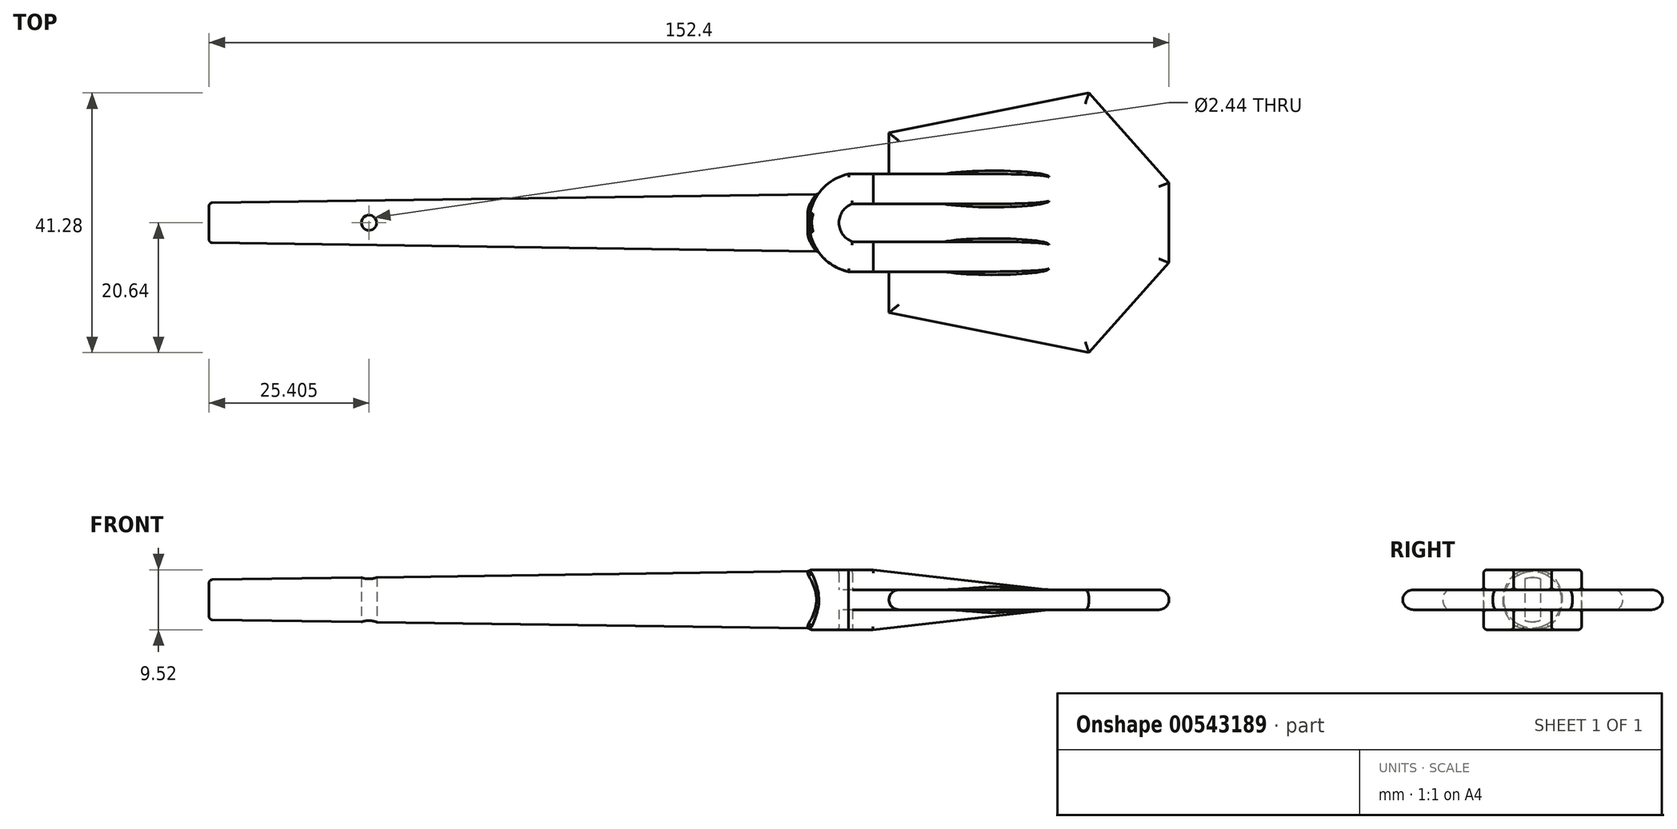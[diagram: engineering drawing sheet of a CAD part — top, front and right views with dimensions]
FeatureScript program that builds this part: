
annotation { "Feature Type Name" : "Feature", "Feature Type Description" : "" }
export const myFeature = defineFeature(function(context is Context, id is Id, definition is map)
    precondition{}
    {
        {
            var Q0;
            Q0=qCreatedBy(makeId("Top.planeOp"),FACE);
            var sketch = newSketch(context, id + "F0", { "sketchPlane" : qUnion([Q0])});
            skLineSegment(sketch, "E0", {"start": v(0, 0) * mm, "end": v(-95.25, 0) * mm});
            skLineSegment(sketch, "E1", {"start": v(-95.25, 0) * mm, "end": v(-95.25, 3.17) * mm});
            skLineSegment(sketch, "E2", {"start": v(-95.25, 3.17) * mm, "end": v(1.43, 4.54) * mm});
            skArc(sketch, "E3", {"start": v(6.28, 7.76) * mm, "mid": v(1.77, 5) * mm, "end": v(0, 0) * mm});
            skLineSegment(sketch, "E4", {"start": v(6.28, 7.76) * mm, "end": v(38.1, 7.76) * mm});
            skLineSegment(sketch, "E5", {"start": v(12.7, 0) * mm, "end": v(12.7, 14.29) * mm});
            skLineSegment(sketch, "E6", {"start": v(12.7, 14.29) * mm, "end": v(44.45, 20.64) * mm});
            skLineSegment(sketch, "E7", {"start": v(44.45, 20.64) * mm, "end": v(57.15, 6.35) * mm});
            skLineSegment(sketch, "E8", {"start": v(57.15, 6.35) * mm, "end": v(57.15, 0) * mm});
            skLineSegment(sketch, "E9.0", {"start": v(6.9, 3) * mm, "end": v(38.1, 3) * mm});
            skArc(sketch, "E9.1", {"start": v(6.9, 3) * mm, "mid": v(5.35, 1.84) * mm, "end": v(4.76, 0) * mm});
            skArc(sketch, "E10.MirrorCS", {"start": v(6.28, -7.76) * mm, "mid": v(1.77, -5) * mm, "end": v(0, 0) * mm});
            skLineSegment(sketch, "E11.MirrorCS", {"start": v(6.28, -7.76) * mm, "end": v(38.1, -7.76) * mm});
            skLineSegment(sketch, "E12.MirrorCS", {"start": v(6.9, -3) * mm, "end": v(38.1, -3) * mm});
            skArc(sketch, "E13.MirrorCS", {"start": v(6.9, -3) * mm, "mid": v(5.35, -1.84) * mm, "end": v(4.76, 0) * mm});
            skLineSegment(sketch, "E14.MirrorCS", {"start": v(12.7, 0) * mm, "end": v(12.7, -14.29) * mm});
            skLineSegment(sketch, "E15.MirrorCS", {"start": v(12.7, -14.29) * mm, "end": v(44.45, -20.64) * mm});
            skLineSegment(sketch, "E16.MirrorCS", {"start": v(57.15, -6.35) * mm, "end": v(57.15, 0) * mm});
            skLineSegment(sketch, "E17.MirrorCS", {"start": v(44.45, -20.64) * mm, "end": v(57.15, -6.35) * mm});
            skLineSegment(sketch, "E18", {"start": v(38.1, 7.76) * mm, "end": v(38.1, 3) * mm});
            skLineSegment(sketch, "E19", {"start": v(38.1, -3) * mm, "end": v(38.1, -7.76) * mm});
            skLineSegment(sketch, "E20.0", {"start": v(-69.85, 0) * mm, "end": v(-69.85, 3.17) * mm});
            skCircle(sketch, "E21", {"center": v(-69.85, 0) * mm, "radius": 0.95 * mm});
            skSolve(sketch);
        }
        {
            var Q0;
            {var subQ5=sQuery(id+"F0.wireOp",EDGE,"E9.1");Q0=makeQuery(id+"F0.imprint","IMPRINT",FACE,{"disambiguationData":[TD([[makeQuery(id+"F0.imprint","IMPRINT",EDGE,{"derivedFrom":subQ5}),-1.0]])]});}
            var Q1;
            {var subQ0=sQuery(id+"F0.wireOp",EDGE,"E19");Q1=makeQuery(id+"F0.imprint","IMPRINT",FACE,{"disambiguationData":[TD([[makeQuery(id+"F0.imprint","IMPRINT",EDGE,{"derivedFrom":subQ0}),-1.0]])]});}
            var Q2;
            {var subQ0=sQuery(id+"F0.wireOp",EDGE,"E18");Q2=makeQuery(id+"F0.imprint","IMPRINT",FACE,{"disambiguationData":[TD([[makeQuery(id+"F0.imprint","IMPRINT",EDGE,{"derivedFrom":subQ0}),-1.0]])]});}
            extrude(context, id + "F1", {"entities" : qUnion([Q0, Q1, Q2]), "depth" : 9.52 * mm, "offsetDistance" : 25.4 * mm, "symmetric" : true});
        }
        {
            var Q0;
            {var subQ13=sQuery(id+"F0.wireOp",EDGE,"E6");Q0=makeQuery(id+"F0.imprint","IMPRINT",FACE,{"disambiguationData":[TD([[makeQuery(id+"F0.imprint","IMPRINT",EDGE,{"derivedFrom":subQ13}),-1.0]])]});}
            var Q1;
            {var subQ4=sQuery(id+"F0.wireOp",EDGE,"E9.1");Q1=makeQuery(id+"F0.imprint","IMPRINT",FACE,{"disambiguationData":[TD([[makeQuery(id+"F0.imprint","IMPRINT",EDGE,{"derivedFrom":subQ4}),1.0]])]});}
            extrude(context, id + "F2", {"entities" : qUnion([Q0, Q1]), "operationType" : NewBodyOperationType.ADD, "depth" : 3.17 * mm, "offsetDistance" : 25.4 * mm, "symmetric" : true});
        }
        {
            var Q0;
            {var subQ0=sQuery(id+"F0.wireOp",EDGE,"E0");Q0=makeQuery(id+"F0.imprint","IMPRINT",FACE,{"disambiguationData":[TD([[makeQuery(id+"F0.imprint","IMPRINT",EDGE,{"derivedFrom":subQ0}),-1.0]])]});}
            var Q1;
            Q1=sQuery(id+"F0.wireOp",EDGE,"E0");
            revolve(context, id + "F3", {"operationType" : NewBodyOperationType.ADD, "entities" : qUnion([Q0]), "axis" : qUnion([Q1]), "revolveType" : RevolveType.FULL});
        }
        {
            var Q0;
            Q0=makeQuery(id+"F1.opExtrude","CAP_EDGE",EDGE,{"disambiguationData":[OSD([sQuery(id+"F0.wireOp",EDGE,"E19")])],"isStart":false});
            var Q1;
            Q1=makeQuery(id+"F1.opExtrude","CAP_EDGE",EDGE,{"disambiguationData":[OSD([sQuery(id+"F0.wireOp",EDGE,"E18")])],"isStart":false});
            chamfer(context, id + "F4", {"entities" : qUnion([Q0, Q1]), "chamferType" : ChamferType.OFFSET_ANGLE, "width" : 3.17 * mm, "oppositeDirection" : false, "angle" : 83.5 * degree, "tangentPropagation" : true});
        }
        {
            var Q0;
            Q0=makeQuery(id+"F1.opExtrude","CAP_EDGE",EDGE,{"disambiguationData":[OSD([sQuery(id+"F0.wireOp",EDGE,"E19")])],"isStart":true});
            var Q1;
            Q1=makeQuery(id+"F1.opExtrude","CAP_EDGE",EDGE,{"disambiguationData":[OSD([sQuery(id+"F0.wireOp",EDGE,"E18")])],"isStart":true});
            chamfer(context, id + "F5", {"entities" : qUnion([Q0, Q1]), "chamferType" : ChamferType.OFFSET_ANGLE, "width" : 27.94 * mm, "oppositeDirection" : false, "angle" : 6.5 * degree, "tangentPropagation" : true});
        }
        {
            var Q0;
            Q0=makeQuery(id+"F1.opExtrude","CAP_EDGE",EDGE,{"disambiguationData":[OSD([sQuery(id+"F0.wireOp",EDGE,"E3"),sQuery(id+"F0.wireOp",EDGE,"E10.MirrorCS")])],"isStart":true});
            var Q1;
            Q1=makeQuery(id+"F1.opExtrude","CAP_EDGE",EDGE,{"disambiguationData":[OSD([sQuery(id+"F0.wireOp",EDGE,"E4")])],"isStart":true});
            var Q2;
            Q2=makeQuery(id+"F1.opExtrude","CAP_EDGE",EDGE,{"disambiguationData":[OSD([sQuery(id+"F0.wireOp",EDGE,"E11.MirrorCS")])],"isStart":true});
            var Q3;
            Q3=makeQuery(id+"F5.opChamfer","BLEND_EDGE",EDGE,{"blendedFrom":[makeQuery(id+"F1.opExtrude","CAP_EDGE",EDGE,{"disambiguationData":[OSD([sQuery(id+"F0.wireOp",EDGE,"E19")])],"isStart":true}),makeQuery(id+"F1.opExtrude","SWEPT_FACE",FACE,{"disambiguationData":[OSD([sQuery(id+"F0.wireOp",EDGE,"E11.MirrorCS")])]})],"blendedInto":[makeQuery(id+"F1.opExtrude","SWEPT_FACE",FACE,{"disambiguationData":[OSD([sQuery(id+"F0.wireOp",EDGE,"E11.MirrorCS")])]})]});
            var Q4;
            Q4=makeQuery(id+"F5.opChamfer","BLEND_EDGE",EDGE,{"blendedFrom":[makeQuery(id+"F1.opExtrude","CAP_EDGE",EDGE,{"disambiguationData":[OSD([sQuery(id+"F0.wireOp",EDGE,"E18")])],"isStart":true}),makeQuery(id+"F1.opExtrude","SWEPT_FACE",FACE,{"disambiguationData":[OSD([sQuery(id+"F0.wireOp",EDGE,"E4")])]})],"blendedInto":[makeQuery(id+"F1.opExtrude","SWEPT_FACE",FACE,{"disambiguationData":[OSD([sQuery(id+"F0.wireOp",EDGE,"E4")])]})]});
            var Q5;
            {var subQ0=sQuery(id+"F0.wireOp",EDGE,"E18");Q5=makeQuery(id+"F5.opChamfer","BLEND_EDGE",EDGE,{"blendedFrom":[makeQuery(id+"F1.opExtrude","CAP_EDGE",EDGE,{"disambiguationData":[OSD([subQ0])],"isStart":true}),makeQuery(id+"F2.opExtrude","CAP_FACE",FACE,{"disambiguationData":[OSD([sQuery(id+"F0.wireOp",EDGE,"E4"),sQuery(id+"F0.wireOp",EDGE,"E5"),sQuery(id+"F0.wireOp",EDGE,"E6"),sQuery(id+"F0.wireOp",EDGE,"E7"),sQuery(id+"F0.wireOp",EDGE,"E8"),sQuery(id+"F0.wireOp",EDGE,"E9.0"),sQuery(id+"F0.wireOp",EDGE,"E9.1"),sQuery(id+"F0.wireOp",EDGE,"E11.MirrorCS"),sQuery(id+"F0.wireOp",EDGE,"E12.MirrorCS"),sQuery(id+"F0.wireOp",EDGE,"E13.MirrorCS"),sQuery(id+"F0.wireOp",EDGE,"E14.MirrorCS"),sQuery(id+"F0.wireOp",EDGE,"E15.MirrorCS"),sQuery(id+"F0.wireOp",EDGE,"E16.MirrorCS"),sQuery(id+"F0.wireOp",EDGE,"E17.MirrorCS"),subQ0,sQuery(id+"F0.wireOp",EDGE,"E19")])],"isStart":true})],"blendedInto":[makeQuery(id+"F2.opExtrude","CAP_FACE",FACE,{"disambiguationData":[OSD([sQuery(id+"F0.wireOp",EDGE,"E4"),sQuery(id+"F0.wireOp",EDGE,"E5"),sQuery(id+"F0.wireOp",EDGE,"E6"),sQuery(id+"F0.wireOp",EDGE,"E7"),sQuery(id+"F0.wireOp",EDGE,"E8"),sQuery(id+"F0.wireOp",EDGE,"E9.0"),sQuery(id+"F0.wireOp",EDGE,"E9.1"),sQuery(id+"F0.wireOp",EDGE,"E11.MirrorCS"),sQuery(id+"F0.wireOp",EDGE,"E12.MirrorCS"),sQuery(id+"F0.wireOp",EDGE,"E13.MirrorCS"),sQuery(id+"F0.wireOp",EDGE,"E14.MirrorCS"),sQuery(id+"F0.wireOp",EDGE,"E15.MirrorCS"),sQuery(id+"F0.wireOp",EDGE,"E16.MirrorCS"),sQuery(id+"F0.wireOp",EDGE,"E17.MirrorCS"),subQ0,sQuery(id+"F0.wireOp",EDGE,"E19")])],"isStart":true})]});}
            var Q6;
            {var subQ0=sQuery(id+"F0.wireOp",EDGE,"E19");var subQ1=sQuery(id+"F0.wireOp",EDGE,"E18");var subQ2=sQuery(id+"F0.wireOp",EDGE,"E13.MirrorCS");var subQ3=sQuery(id+"F0.wireOp",EDGE,"E12.MirrorCS");var subQ4=sQuery(id+"F0.wireOp",EDGE,"E11.MirrorCS");var subQ5=sQuery(id+"F0.wireOp",EDGE,"E9.1");var subQ6=sQuery(id+"F0.wireOp",EDGE,"E9.0");var subQ7=sQuery(id+"F0.wireOp",EDGE,"E4");Q6=makeQuery(id+"F5.opChamfer","BLEND_EDGE",EDGE,{"blendedFrom":[makeQuery(id+"F1.opExtrude","CAP_EDGE",EDGE,{"disambiguationData":[OSD([subQ1])],"isStart":true}),makeQuery(id+"F2.boolean.opBoolean","SPLIT",FACE,{"disambiguationData":[TD([makeQuery(id+"F1.opExtrude","CAP_FACE",FACE,{"disambiguationData":[OSD([sQuery(id+"F0.wireOp",EDGE,"E3"),subQ7,subQ6,subQ5,sQuery(id+"F0.wireOp",EDGE,"E10.MirrorCS"),subQ4,subQ3,subQ2,subQ1,subQ0])],"isStart":true})])],"derivedFrom":makeQuery(id+"F1.opExtrude","SWEPT_FACE",FACE,{"disambiguationData":[OSD([subQ6])]})})],"blendedInto":[makeQuery(id+"F2.boolean.opBoolean","SPLIT",FACE,{"disambiguationData":[TD([makeQuery(id+"F1.opExtrude","CAP_FACE",FACE,{"disambiguationData":[OSD([sQuery(id+"F0.wireOp",EDGE,"E3"),subQ7,subQ6,subQ5,sQuery(id+"F0.wireOp",EDGE,"E10.MirrorCS"),subQ4,subQ3,subQ2,subQ1,subQ0])],"isStart":true})])],"derivedFrom":makeQuery(id+"F1.opExtrude","SWEPT_FACE",FACE,{"disambiguationData":[OSD([subQ6])]})})]});}
            var Q7;
            Q7=makeQuery(id+"F1.opExtrude","CAP_EDGE",EDGE,{"disambiguationData":[OSD([sQuery(id+"F0.wireOp",EDGE,"E9.0")])],"isStart":true});
            var Q8;
            Q8=makeQuery(id+"F1.opExtrude","CAP_EDGE",EDGE,{"disambiguationData":[OSD([sQuery(id+"F0.wireOp",EDGE,"E9.1"),sQuery(id+"F0.wireOp",EDGE,"E13.MirrorCS")])],"isStart":true});
            var Q9;
            Q9=makeQuery(id+"F1.opExtrude","CAP_EDGE",EDGE,{"disambiguationData":[OSD([sQuery(id+"F0.wireOp",EDGE,"E12.MirrorCS")])],"isStart":true});
            var Q10;
            {var subQ0=sQuery(id+"F0.wireOp",EDGE,"E19");var subQ1=sQuery(id+"F0.wireOp",EDGE,"E18");var subQ2=sQuery(id+"F0.wireOp",EDGE,"E13.MirrorCS");var subQ3=sQuery(id+"F0.wireOp",EDGE,"E12.MirrorCS");var subQ4=sQuery(id+"F0.wireOp",EDGE,"E11.MirrorCS");var subQ5=sQuery(id+"F0.wireOp",EDGE,"E9.1");var subQ6=sQuery(id+"F0.wireOp",EDGE,"E9.0");var subQ7=sQuery(id+"F0.wireOp",EDGE,"E4");Q10=makeQuery(id+"F5.opChamfer","BLEND_EDGE",EDGE,{"blendedFrom":[makeQuery(id+"F1.opExtrude","CAP_EDGE",EDGE,{"disambiguationData":[OSD([subQ0])],"isStart":true}),makeQuery(id+"F2.boolean.opBoolean","SPLIT",FACE,{"disambiguationData":[TD([makeQuery(id+"F1.opExtrude","CAP_FACE",FACE,{"disambiguationData":[OSD([sQuery(id+"F0.wireOp",EDGE,"E3"),subQ7,subQ6,subQ5,sQuery(id+"F0.wireOp",EDGE,"E10.MirrorCS"),subQ4,subQ3,subQ2,subQ1,subQ0])],"isStart":true})])],"derivedFrom":makeQuery(id+"F1.opExtrude","SWEPT_FACE",FACE,{"disambiguationData":[OSD([subQ3])]})})],"blendedInto":[makeQuery(id+"F2.boolean.opBoolean","SPLIT",FACE,{"disambiguationData":[TD([makeQuery(id+"F1.opExtrude","CAP_FACE",FACE,{"disambiguationData":[OSD([sQuery(id+"F0.wireOp",EDGE,"E3"),subQ7,subQ6,subQ5,sQuery(id+"F0.wireOp",EDGE,"E10.MirrorCS"),subQ4,subQ3,subQ2,subQ1,subQ0])],"isStart":true})])],"derivedFrom":makeQuery(id+"F1.opExtrude","SWEPT_FACE",FACE,{"disambiguationData":[OSD([subQ3])]})})]});}
            var Q11;
            {var subQ0=sQuery(id+"F0.wireOp",EDGE,"E19");Q11=makeQuery(id+"F5.opChamfer","BLEND_EDGE",EDGE,{"blendedFrom":[makeQuery(id+"F1.opExtrude","CAP_EDGE",EDGE,{"disambiguationData":[OSD([subQ0])],"isStart":true}),makeQuery(id+"F2.opExtrude","CAP_FACE",FACE,{"disambiguationData":[OSD([sQuery(id+"F0.wireOp",EDGE,"E4"),sQuery(id+"F0.wireOp",EDGE,"E5"),sQuery(id+"F0.wireOp",EDGE,"E6"),sQuery(id+"F0.wireOp",EDGE,"E7"),sQuery(id+"F0.wireOp",EDGE,"E8"),sQuery(id+"F0.wireOp",EDGE,"E9.0"),sQuery(id+"F0.wireOp",EDGE,"E9.1"),sQuery(id+"F0.wireOp",EDGE,"E11.MirrorCS"),sQuery(id+"F0.wireOp",EDGE,"E12.MirrorCS"),sQuery(id+"F0.wireOp",EDGE,"E13.MirrorCS"),sQuery(id+"F0.wireOp",EDGE,"E14.MirrorCS"),sQuery(id+"F0.wireOp",EDGE,"E15.MirrorCS"),sQuery(id+"F0.wireOp",EDGE,"E16.MirrorCS"),sQuery(id+"F0.wireOp",EDGE,"E17.MirrorCS"),sQuery(id+"F0.wireOp",EDGE,"E18"),subQ0])],"isStart":true})],"blendedInto":[makeQuery(id+"F2.opExtrude","CAP_FACE",FACE,{"disambiguationData":[OSD([sQuery(id+"F0.wireOp",EDGE,"E4"),sQuery(id+"F0.wireOp",EDGE,"E5"),sQuery(id+"F0.wireOp",EDGE,"E6"),sQuery(id+"F0.wireOp",EDGE,"E7"),sQuery(id+"F0.wireOp",EDGE,"E8"),sQuery(id+"F0.wireOp",EDGE,"E9.0"),sQuery(id+"F0.wireOp",EDGE,"E9.1"),sQuery(id+"F0.wireOp",EDGE,"E11.MirrorCS"),sQuery(id+"F0.wireOp",EDGE,"E12.MirrorCS"),sQuery(id+"F0.wireOp",EDGE,"E13.MirrorCS"),sQuery(id+"F0.wireOp",EDGE,"E14.MirrorCS"),sQuery(id+"F0.wireOp",EDGE,"E15.MirrorCS"),sQuery(id+"F0.wireOp",EDGE,"E16.MirrorCS"),sQuery(id+"F0.wireOp",EDGE,"E17.MirrorCS"),sQuery(id+"F0.wireOp",EDGE,"E18"),subQ0])],"isStart":true})]});}
            var Q12;
            Q12=makeQuery(id+"F1.opExtrude","CAP_EDGE",EDGE,{"disambiguationData":[OSD([sQuery(id+"F0.wireOp",EDGE,"E3"),sQuery(id+"F0.wireOp",EDGE,"E10.MirrorCS")])],"isStart":false});
            var Q13;
            Q13=makeQuery(id+"F1.opExtrude","CAP_EDGE",EDGE,{"disambiguationData":[OSD([sQuery(id+"F0.wireOp",EDGE,"E4")])],"isStart":false});
            var Q14;
            Q14=makeQuery(id+"F4.opChamfer","BLEND_EDGE",EDGE,{"blendedFrom":[makeQuery(id+"F1.opExtrude","CAP_EDGE",EDGE,{"disambiguationData":[OSD([sQuery(id+"F0.wireOp",EDGE,"E18")])],"isStart":false}),makeQuery(id+"F1.opExtrude","SWEPT_FACE",FACE,{"disambiguationData":[OSD([sQuery(id+"F0.wireOp",EDGE,"E4")])]})],"blendedInto":[makeQuery(id+"F1.opExtrude","SWEPT_FACE",FACE,{"disambiguationData":[OSD([sQuery(id+"F0.wireOp",EDGE,"E4")])]})]});
            var Q15;
            {var subQ0=sQuery(id+"F0.wireOp",EDGE,"E18");Q15=makeQuery(id+"F4.opChamfer","BLEND_EDGE",EDGE,{"blendedFrom":[makeQuery(id+"F1.opExtrude","CAP_EDGE",EDGE,{"disambiguationData":[OSD([subQ0])],"isStart":false}),makeQuery(id+"F2.opExtrude","CAP_FACE",FACE,{"disambiguationData":[OSD([sQuery(id+"F0.wireOp",EDGE,"E4"),sQuery(id+"F0.wireOp",EDGE,"E5"),sQuery(id+"F0.wireOp",EDGE,"E6"),sQuery(id+"F0.wireOp",EDGE,"E7"),sQuery(id+"F0.wireOp",EDGE,"E8"),sQuery(id+"F0.wireOp",EDGE,"E9.0"),sQuery(id+"F0.wireOp",EDGE,"E9.1"),sQuery(id+"F0.wireOp",EDGE,"E11.MirrorCS"),sQuery(id+"F0.wireOp",EDGE,"E12.MirrorCS"),sQuery(id+"F0.wireOp",EDGE,"E13.MirrorCS"),sQuery(id+"F0.wireOp",EDGE,"E14.MirrorCS"),sQuery(id+"F0.wireOp",EDGE,"E15.MirrorCS"),sQuery(id+"F0.wireOp",EDGE,"E16.MirrorCS"),sQuery(id+"F0.wireOp",EDGE,"E17.MirrorCS"),subQ0,sQuery(id+"F0.wireOp",EDGE,"E19")])],"isStart":false})],"blendedInto":[makeQuery(id+"F2.opExtrude","CAP_FACE",FACE,{"disambiguationData":[OSD([sQuery(id+"F0.wireOp",EDGE,"E4"),sQuery(id+"F0.wireOp",EDGE,"E5"),sQuery(id+"F0.wireOp",EDGE,"E6"),sQuery(id+"F0.wireOp",EDGE,"E7"),sQuery(id+"F0.wireOp",EDGE,"E8"),sQuery(id+"F0.wireOp",EDGE,"E9.0"),sQuery(id+"F0.wireOp",EDGE,"E9.1"),sQuery(id+"F0.wireOp",EDGE,"E11.MirrorCS"),sQuery(id+"F0.wireOp",EDGE,"E12.MirrorCS"),sQuery(id+"F0.wireOp",EDGE,"E13.MirrorCS"),sQuery(id+"F0.wireOp",EDGE,"E14.MirrorCS"),sQuery(id+"F0.wireOp",EDGE,"E15.MirrorCS"),sQuery(id+"F0.wireOp",EDGE,"E16.MirrorCS"),sQuery(id+"F0.wireOp",EDGE,"E17.MirrorCS"),subQ0,sQuery(id+"F0.wireOp",EDGE,"E19")])],"isStart":false})]});}
            var Q16;
            {var subQ0=sQuery(id+"F0.wireOp",EDGE,"E19");var subQ1=sQuery(id+"F0.wireOp",EDGE,"E18");var subQ2=sQuery(id+"F0.wireOp",EDGE,"E13.MirrorCS");var subQ3=sQuery(id+"F0.wireOp",EDGE,"E12.MirrorCS");var subQ4=sQuery(id+"F0.wireOp",EDGE,"E11.MirrorCS");var subQ5=sQuery(id+"F0.wireOp",EDGE,"E9.1");var subQ6=sQuery(id+"F0.wireOp",EDGE,"E9.0");var subQ7=sQuery(id+"F0.wireOp",EDGE,"E4");Q16=makeQuery(id+"F4.opChamfer","BLEND_EDGE",EDGE,{"blendedFrom":[makeQuery(id+"F1.opExtrude","CAP_EDGE",EDGE,{"disambiguationData":[OSD([subQ1])],"isStart":false}),makeQuery(id+"F2.boolean.opBoolean","SPLIT",FACE,{"disambiguationData":[TD([makeQuery(id+"F1.opExtrude","CAP_FACE",FACE,{"disambiguationData":[OSD([sQuery(id+"F0.wireOp",EDGE,"E3"),subQ7,subQ6,subQ5,sQuery(id+"F0.wireOp",EDGE,"E10.MirrorCS"),subQ4,subQ3,subQ2,subQ1,subQ0])],"isStart":false})])],"derivedFrom":makeQuery(id+"F1.opExtrude","SWEPT_FACE",FACE,{"disambiguationData":[OSD([subQ6])]})})],"blendedInto":[makeQuery(id+"F2.boolean.opBoolean","SPLIT",FACE,{"disambiguationData":[TD([makeQuery(id+"F1.opExtrude","CAP_FACE",FACE,{"disambiguationData":[OSD([sQuery(id+"F0.wireOp",EDGE,"E3"),subQ7,subQ6,subQ5,sQuery(id+"F0.wireOp",EDGE,"E10.MirrorCS"),subQ4,subQ3,subQ2,subQ1,subQ0])],"isStart":false})])],"derivedFrom":makeQuery(id+"F1.opExtrude","SWEPT_FACE",FACE,{"disambiguationData":[OSD([subQ6])]})})]});}
            var Q17;
            Q17=makeQuery(id+"F1.opExtrude","CAP_EDGE",EDGE,{"disambiguationData":[OSD([sQuery(id+"F0.wireOp",EDGE,"E9.0")])],"isStart":false});
            var Q18;
            Q18=makeQuery(id+"F1.opExtrude","CAP_EDGE",EDGE,{"disambiguationData":[OSD([sQuery(id+"F0.wireOp",EDGE,"E9.1"),sQuery(id+"F0.wireOp",EDGE,"E13.MirrorCS")])],"isStart":false});
            var Q19;
            Q19=makeQuery(id+"F1.opExtrude","CAP_EDGE",EDGE,{"disambiguationData":[OSD([sQuery(id+"F0.wireOp",EDGE,"E12.MirrorCS")])],"isStart":false});
            var Q20;
            {var subQ0=sQuery(id+"F0.wireOp",EDGE,"E19");var subQ1=sQuery(id+"F0.wireOp",EDGE,"E18");var subQ2=sQuery(id+"F0.wireOp",EDGE,"E13.MirrorCS");var subQ3=sQuery(id+"F0.wireOp",EDGE,"E12.MirrorCS");var subQ4=sQuery(id+"F0.wireOp",EDGE,"E11.MirrorCS");var subQ5=sQuery(id+"F0.wireOp",EDGE,"E9.1");var subQ6=sQuery(id+"F0.wireOp",EDGE,"E9.0");var subQ7=sQuery(id+"F0.wireOp",EDGE,"E4");Q20=makeQuery(id+"F4.opChamfer","BLEND_EDGE",EDGE,{"blendedFrom":[makeQuery(id+"F1.opExtrude","CAP_EDGE",EDGE,{"disambiguationData":[OSD([subQ0])],"isStart":false}),makeQuery(id+"F2.boolean.opBoolean","SPLIT",FACE,{"disambiguationData":[TD([makeQuery(id+"F1.opExtrude","CAP_FACE",FACE,{"disambiguationData":[OSD([sQuery(id+"F0.wireOp",EDGE,"E3"),subQ7,subQ6,subQ5,sQuery(id+"F0.wireOp",EDGE,"E10.MirrorCS"),subQ4,subQ3,subQ2,subQ1,subQ0])],"isStart":false})])],"derivedFrom":makeQuery(id+"F1.opExtrude","SWEPT_FACE",FACE,{"disambiguationData":[OSD([subQ3])]})})],"blendedInto":[makeQuery(id+"F2.boolean.opBoolean","SPLIT",FACE,{"disambiguationData":[TD([makeQuery(id+"F1.opExtrude","CAP_FACE",FACE,{"disambiguationData":[OSD([sQuery(id+"F0.wireOp",EDGE,"E3"),subQ7,subQ6,subQ5,sQuery(id+"F0.wireOp",EDGE,"E10.MirrorCS"),subQ4,subQ3,subQ2,subQ1,subQ0])],"isStart":false})])],"derivedFrom":makeQuery(id+"F1.opExtrude","SWEPT_FACE",FACE,{"disambiguationData":[OSD([subQ3])]})})]});}
            var Q21;
            {var subQ0=sQuery(id+"F0.wireOp",EDGE,"E19");Q21=makeQuery(id+"F4.opChamfer","BLEND_EDGE",EDGE,{"blendedFrom":[makeQuery(id+"F1.opExtrude","CAP_EDGE",EDGE,{"disambiguationData":[OSD([subQ0])],"isStart":false}),makeQuery(id+"F2.opExtrude","CAP_FACE",FACE,{"disambiguationData":[OSD([sQuery(id+"F0.wireOp",EDGE,"E4"),sQuery(id+"F0.wireOp",EDGE,"E5"),sQuery(id+"F0.wireOp",EDGE,"E6"),sQuery(id+"F0.wireOp",EDGE,"E7"),sQuery(id+"F0.wireOp",EDGE,"E8"),sQuery(id+"F0.wireOp",EDGE,"E9.0"),sQuery(id+"F0.wireOp",EDGE,"E9.1"),sQuery(id+"F0.wireOp",EDGE,"E11.MirrorCS"),sQuery(id+"F0.wireOp",EDGE,"E12.MirrorCS"),sQuery(id+"F0.wireOp",EDGE,"E13.MirrorCS"),sQuery(id+"F0.wireOp",EDGE,"E14.MirrorCS"),sQuery(id+"F0.wireOp",EDGE,"E15.MirrorCS"),sQuery(id+"F0.wireOp",EDGE,"E16.MirrorCS"),sQuery(id+"F0.wireOp",EDGE,"E17.MirrorCS"),sQuery(id+"F0.wireOp",EDGE,"E18"),subQ0])],"isStart":false})],"blendedInto":[makeQuery(id+"F2.opExtrude","CAP_FACE",FACE,{"disambiguationData":[OSD([sQuery(id+"F0.wireOp",EDGE,"E4"),sQuery(id+"F0.wireOp",EDGE,"E5"),sQuery(id+"F0.wireOp",EDGE,"E6"),sQuery(id+"F0.wireOp",EDGE,"E7"),sQuery(id+"F0.wireOp",EDGE,"E8"),sQuery(id+"F0.wireOp",EDGE,"E9.0"),sQuery(id+"F0.wireOp",EDGE,"E9.1"),sQuery(id+"F0.wireOp",EDGE,"E11.MirrorCS"),sQuery(id+"F0.wireOp",EDGE,"E12.MirrorCS"),sQuery(id+"F0.wireOp",EDGE,"E13.MirrorCS"),sQuery(id+"F0.wireOp",EDGE,"E14.MirrorCS"),sQuery(id+"F0.wireOp",EDGE,"E15.MirrorCS"),sQuery(id+"F0.wireOp",EDGE,"E16.MirrorCS"),sQuery(id+"F0.wireOp",EDGE,"E17.MirrorCS"),sQuery(id+"F0.wireOp",EDGE,"E18"),subQ0])],"isStart":false})]});}
            var Q22;
            Q22=makeQuery(id+"F4.opChamfer","BLEND_EDGE",EDGE,{"blendedFrom":[makeQuery(id+"F1.opExtrude","CAP_EDGE",EDGE,{"disambiguationData":[OSD([sQuery(id+"F0.wireOp",EDGE,"E19")])],"isStart":false}),makeQuery(id+"F1.opExtrude","SWEPT_FACE",FACE,{"disambiguationData":[OSD([sQuery(id+"F0.wireOp",EDGE,"E11.MirrorCS")])]})],"blendedInto":[makeQuery(id+"F1.opExtrude","SWEPT_FACE",FACE,{"disambiguationData":[OSD([sQuery(id+"F0.wireOp",EDGE,"E11.MirrorCS")])]})]});
            var Q23;
            Q23=makeQuery(id+"F1.opExtrude","CAP_EDGE",EDGE,{"disambiguationData":[OSD([sQuery(id+"F0.wireOp",EDGE,"E11.MirrorCS")])],"isStart":false});
            fillet(context, id + "F6", {"entities" : qUnion([Q0, Q1, Q2, Q3, Q4, Q5, Q6, Q7, Q8, Q9, Q10, Q11, Q12, Q13, Q14, Q15, Q16, Q17, Q18, Q19, Q20, Q21, Q22, Q23]), "radius" : 0.5 * mm, "tangentPropagation" : true, "allowEdgeOverflow" : false});
        }
        {
            var Q0;
            Q0=makeQuery(id+"F2.opExtrude","SWEPT_EDGE",EDGE,{"disambiguationData":[OSD([sQuery(id+"F0.wireOp",EDGE,"E11.MirrorCS"),sQuery(id+"F0.wireOp",EDGE,"E14.MirrorCS")])]});
            var Q1;
            Q1=makeQuery(id+"F2.opExtrude","SWEPT_EDGE",EDGE,{"disambiguationData":[OSD([sQuery(id+"F0.wireOp",EDGE,"E4"),sQuery(id+"F0.wireOp",EDGE,"E5")])]});
            var Q2;
            Q2=makeQuery(id+"F3.boolean.opBoolean","INTERSECT",EDGE,{"derivedFrom":[makeQuery(id+"F1.opExtrude","SWEPT_FACE",FACE,{"disambiguationData":[OSD([sQuery(id+"F0.wireOp",EDGE,"E3"),sQuery(id+"F0.wireOp",EDGE,"E10.MirrorCS")])]}),makeQuery(id+"F3.opRevolve","SWEPT_FACE",FACE,{"disambiguationData":[OSD([sQuery(id+"F0.wireOp",EDGE,"E2")])]})]});
            fillet(context, id + "F7", {"entities" : qUnion([Q0, Q1, Q2]), "radius" : 0.5 * mm, "tangentPropagation" : true, "allowEdgeOverflow" : false});
        }
        {
            var Q0;
            Q0=makeQuery(id+"F2.opExtrude","CAP_EDGE",EDGE,{"disambiguationData":[OSD([sQuery(id+"F0.wireOp",EDGE,"E5")])],"isStart":true});
            var Q1;
            Q1=makeQuery(id+"F2.opExtrude","CAP_EDGE",EDGE,{"disambiguationData":[OSD([sQuery(id+"F0.wireOp",EDGE,"E6")])],"isStart":true});
            var Q2;
            Q2=makeQuery(id+"F2.opExtrude","CAP_EDGE",EDGE,{"disambiguationData":[OSD([sQuery(id+"F0.wireOp",EDGE,"E7")])],"isStart":true});
            var Q3;
            Q3=makeQuery(id+"F2.opExtrude","CAP_EDGE",EDGE,{"disambiguationData":[OSD([sQuery(id+"F0.wireOp",EDGE,"E8"),sQuery(id+"F0.wireOp",EDGE,"E16.MirrorCS")])],"isStart":true});
            var Q4;
            Q4=makeQuery(id+"F2.opExtrude","CAP_EDGE",EDGE,{"disambiguationData":[OSD([sQuery(id+"F0.wireOp",EDGE,"E17.MirrorCS")])],"isStart":true});
            var Q5;
            Q5=makeQuery(id+"F2.opExtrude","CAP_EDGE",EDGE,{"disambiguationData":[OSD([sQuery(id+"F0.wireOp",EDGE,"E15.MirrorCS")])],"isStart":true});
            var Q6;
            Q6=makeQuery(id+"F2.opExtrude","CAP_EDGE",EDGE,{"disambiguationData":[OSD([sQuery(id+"F0.wireOp",EDGE,"E14.MirrorCS")])],"isStart":true});
            var Q7;
            Q7=makeQuery(id+"F2.opExtrude","CAP_EDGE",EDGE,{"disambiguationData":[OSD([sQuery(id+"F0.wireOp",EDGE,"E5")])],"isStart":false});
            var Q8;
            Q8=makeQuery(id+"F2.opExtrude","CAP_EDGE",EDGE,{"disambiguationData":[OSD([sQuery(id+"F0.wireOp",EDGE,"E6")])],"isStart":false});
            var Q9;
            Q9=makeQuery(id+"F2.opExtrude","CAP_EDGE",EDGE,{"disambiguationData":[OSD([sQuery(id+"F0.wireOp",EDGE,"E7")])],"isStart":false});
            var Q10;
            Q10=makeQuery(id+"F2.opExtrude","CAP_EDGE",EDGE,{"disambiguationData":[OSD([sQuery(id+"F0.wireOp",EDGE,"E8"),sQuery(id+"F0.wireOp",EDGE,"E16.MirrorCS")])],"isStart":false});
            var Q11;
            Q11=makeQuery(id+"F2.opExtrude","CAP_EDGE",EDGE,{"disambiguationData":[OSD([sQuery(id+"F0.wireOp",EDGE,"E17.MirrorCS")])],"isStart":false});
            var Q12;
            Q12=makeQuery(id+"F2.opExtrude","CAP_EDGE",EDGE,{"disambiguationData":[OSD([sQuery(id+"F0.wireOp",EDGE,"E15.MirrorCS")])],"isStart":false});
            var Q13;
            Q13=makeQuery(id+"F2.opExtrude","CAP_EDGE",EDGE,{"disambiguationData":[OSD([sQuery(id+"F0.wireOp",EDGE,"E14.MirrorCS")])],"isStart":false});
            fillet(context, id + "F8", {"entities" : qUnion([Q0, Q1, Q2, Q3, Q4, Q5, Q6, Q7, Q8, Q9, Q10, Q11, Q12, Q13]), "radius" : 1.59 * mm, "tangentPropagation" : true, "allowEdgeOverflow" : false});
        }
        {
            var Q0;
            Q0=makeQuery(id+"F3.opRevolve","SWEPT_EDGE",EDGE,{"disambiguationData":[OSD([sQuery(id+"F0.wireOp",EDGE,"E1"),sQuery(id+"F0.wireOp",EDGE,"E2")])]});
            fillet(context, id + "F9", {"entities" : qUnion([Q0]), "radius" : 0.5 * mm, "tangentPropagation" : true, "allowEdgeOverflow" : false});
        }
        {
            var Q0;
            Q0=qCreatedBy(makeId("Top.planeOp"),FACE);
            cPlane(context, id + "F10", {"entities" : qUnion([Q0]), "cplaneType" : CPlaneType.OFFSET, "offset" : 3.8 * mm, "width" : 152.4 * mm, "height" : 152.4 * mm});
        }
        {
            var Q0;
            Q0=qCreatedBy(id+"F10.planeOp",FACE);
            var sketch = newSketch(context, id + "F11", { "sketchPlane" : qUnion([Q0])});
            skCircle(sketch, "E22", {"center": v(-69.85, 0) * mm, "radius": 0.96 * mm});
            skSolve(sketch);
        }
        {
            var Q0;
            Q0=sQuery(id+"F11.wireOp",VERTEX,"E22.center");
            var Q1;
            Q1=makeQuery(id+"F1.opExtrude","SWEPT_BODY",BODY,{"disambiguationData":[OSD([sQuery(id+"F0.wireOp",EDGE,"E3"),sQuery(id+"F0.wireOp",EDGE,"E4"),sQuery(id+"F0.wireOp",EDGE,"E9.0"),sQuery(id+"F0.wireOp",EDGE,"E9.1"),sQuery(id+"F0.wireOp",EDGE,"E10.MirrorCS"),sQuery(id+"F0.wireOp",EDGE,"E11.MirrorCS"),sQuery(id+"F0.wireOp",EDGE,"E12.MirrorCS"),sQuery(id+"F0.wireOp",EDGE,"E13.MirrorCS"),sQuery(id+"F0.wireOp",EDGE,"E18"),sQuery(id+"F0.wireOp",EDGE,"E19")])]});
            hole(context, id + "F12", {"style" : HoleStyle.SIMPLE, "endStyle" : HoleEndStyle.THROUGH, "standardTappedOrClearance" : lookupTablePath({ "standard" : "ANSI", "fit" : "Normal (ASME)", "size" : "#2", "type" : "Clearance" }), "standardBlindInLast" : lookupTablePath({ "fit" : "Free", "standard" : "ANSI", "size" : "#2", "type" : "Clearance" }), "holeDiameter" : 2.44 * mm, "isTappedThrough" : true, "tappedDepth" : 12.7 * mm, "tapClearance" : 3, "locations" : qUnion([Q0]), "scope" : qUnion([Q1])});
        }
    });
